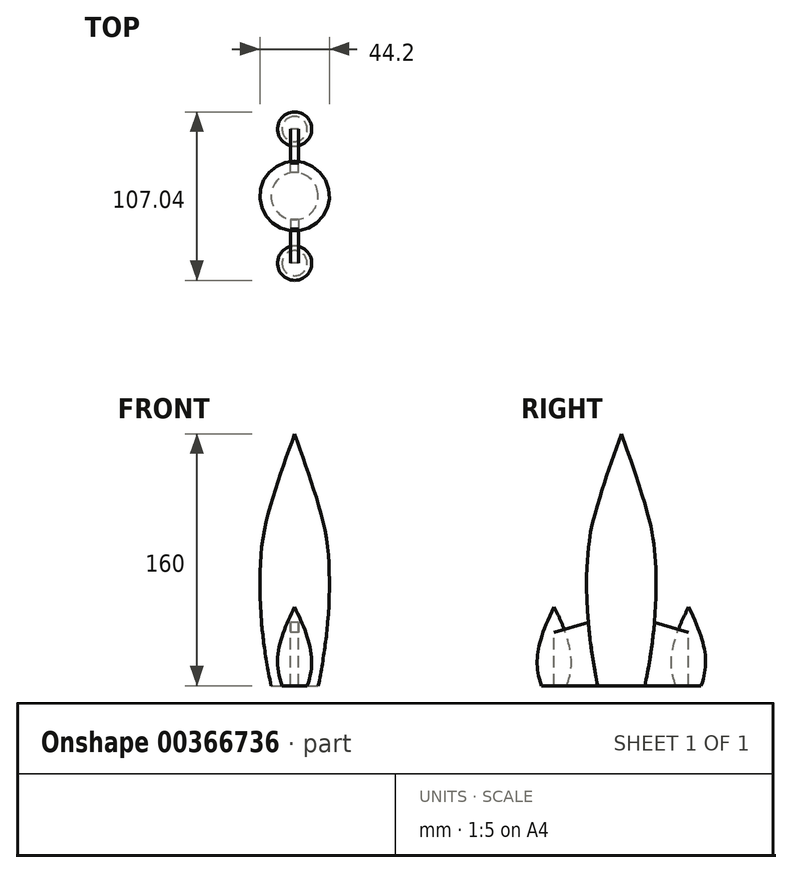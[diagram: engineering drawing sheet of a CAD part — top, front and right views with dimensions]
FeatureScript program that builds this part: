
annotation { "Feature Type Name" : "Feature", "Feature Type Description" : "" }
export const myFeature = defineFeature(function(context is Context, id is Id, definition is map)
    precondition{}
    {
        {
            var Q0;
            Q0=qCreatedBy(makeId("Right.planeOp"),FACE);
            var sketch = newSketch(context, id + "F0", { "sketchPlane" : qUnion([Q0])});
            skLineSegment(sketch, "E0", {"start": v(0, 0) * mm, "end": v(0, 160) * mm});
            skLineSegment(sketch, "E1", {"start": v(0, 0) * mm, "end": v(15, 0) * mm});
            skFitSpline(sketch, "E2", {"points": [v(15, 0) * mm, v(21.66, 79.35) * mm, v(0, 160) * mm], "startDerivative": vector(43.24, 210.96) * mm, "endDerivative": vector(-103.35, 290.24) * mm});
            skLineSegment(sketch, "E3", {"start": v(42.65, 0) * mm, "end": v(42.65, 50) * mm});
            skPoint(sketch, "E3.startSnap0", {"position": v(7.5, 0) * mm});
            skLineSegment(sketch, "E4", {"start": v(42.65, 0) * mm, "end": v(50.65, 0) * mm});
            skFitSpline(sketch, "E5", {"points": [v(50.65, 0) * mm, v(53.23, 19.64) * mm, v(42.65, 50) * mm], "startDerivative": vector(18.29, 51.33) * mm, "endDerivative": vector(-34.5, 68.91) * mm});
            skLineSegment(sketch, "E6", {"start": v(21, 40.27) * mm, "end": v(42.65, 33.96) * mm});
            skLineSegment(sketch, "E7", {"start": v(15, 0) * mm, "end": v(42.65, 0) * mm});
            skSolve(sketch);
        }
        {
            var Q0;
            Q0=makeQuery(id+"F0.imprint","IMPRINT",FACE,{"disambiguationData":[TD([[makeQuery(id+"F0.imprint","IMPRINT",EDGE,{"derivedFrom":sQuery(id+"F0.wireOp",EDGE,"E0")}),-1.0]])]});
            var Q1;
            Q1=sQuery(id+"F0.wireOp",EDGE,"E0");
            revolve(context, id + "F1", {"entities" : qUnion([Q0]), "axis" : qUnion([Q1]), "revolveType" : RevolveType.FULL});
        }
        {
            var Q0;
            Q0=makeQuery(id+"F0.imprint","IMPRINT",FACE,{"disambiguationData":[TD([[makeQuery(id+"F0.imprint","IMPRINT",EDGE,{"derivedFrom":sQuery(id+"F0.wireOp",EDGE,"E3")}),-1.0]])]});
            var Q1;
            Q1=sQuery(id+"F0.wireOp",EDGE,"E3");
            revolve(context, id + "F2", {"entities" : qUnion([Q0]), "axis" : qUnion([Q1]), "revolveType" : RevolveType.FULL});
        }
        {
            var Q0;
            Q0=makeQuery(id+"F2.opRevolve","SWEPT_BODY",BODY,{"disambiguationData":[OSD([sQuery(id+"F0.wireOp",EDGE,"E3"),sQuery(id+"F0.wireOp",EDGE,"E4"),sQuery(id+"F0.wireOp",EDGE,"E5")])]});
            var Q1;
            Q1=qCreatedBy(makeId("Front.planeOp"),FACE);
            mirror(context, id + "F3", {"entities" : qUnion([Q0]), "mirrorPlane" : qUnion([Q1])});
        }
        {
            var Q0;
            {var subQ2=sQuery(id+"F0.wireOp",EDGE,"E6");Q0=makeQuery(id+"F0.imprint","IMPRINT",FACE,{"disambiguationData":[TD([[makeQuery(id+"F0.imprint","IMPRINT",EDGE,{"derivedFrom":subQ2}),-1.0]])]});}
            extrude(context, id + "F4", {"entities" : qUnion([Q0]), "endBound" : BoundingType.SYMMETRIC, "depth" : 5 * mm});
        }
        {
            var Q0;
            Q0=makeQuery(id+"F4.opExtrude","SWEPT_BODY",BODY,{"disambiguationData":[OSD([sQuery(id+"F0.wireOp",EDGE,"E2"),sQuery(id+"F0.wireOp",EDGE,"E3"),sQuery(id+"F0.wireOp",EDGE,"E6"),sQuery(id+"F0.wireOp",EDGE,"E7")])]});
            var Q1;
            Q1=qCreatedBy(makeId("Front.planeOp"),FACE);
            mirror(context, id + "F5", {"entities" : qUnion([Q0]), "mirrorPlane" : qUnion([Q1])});
        }
    });
